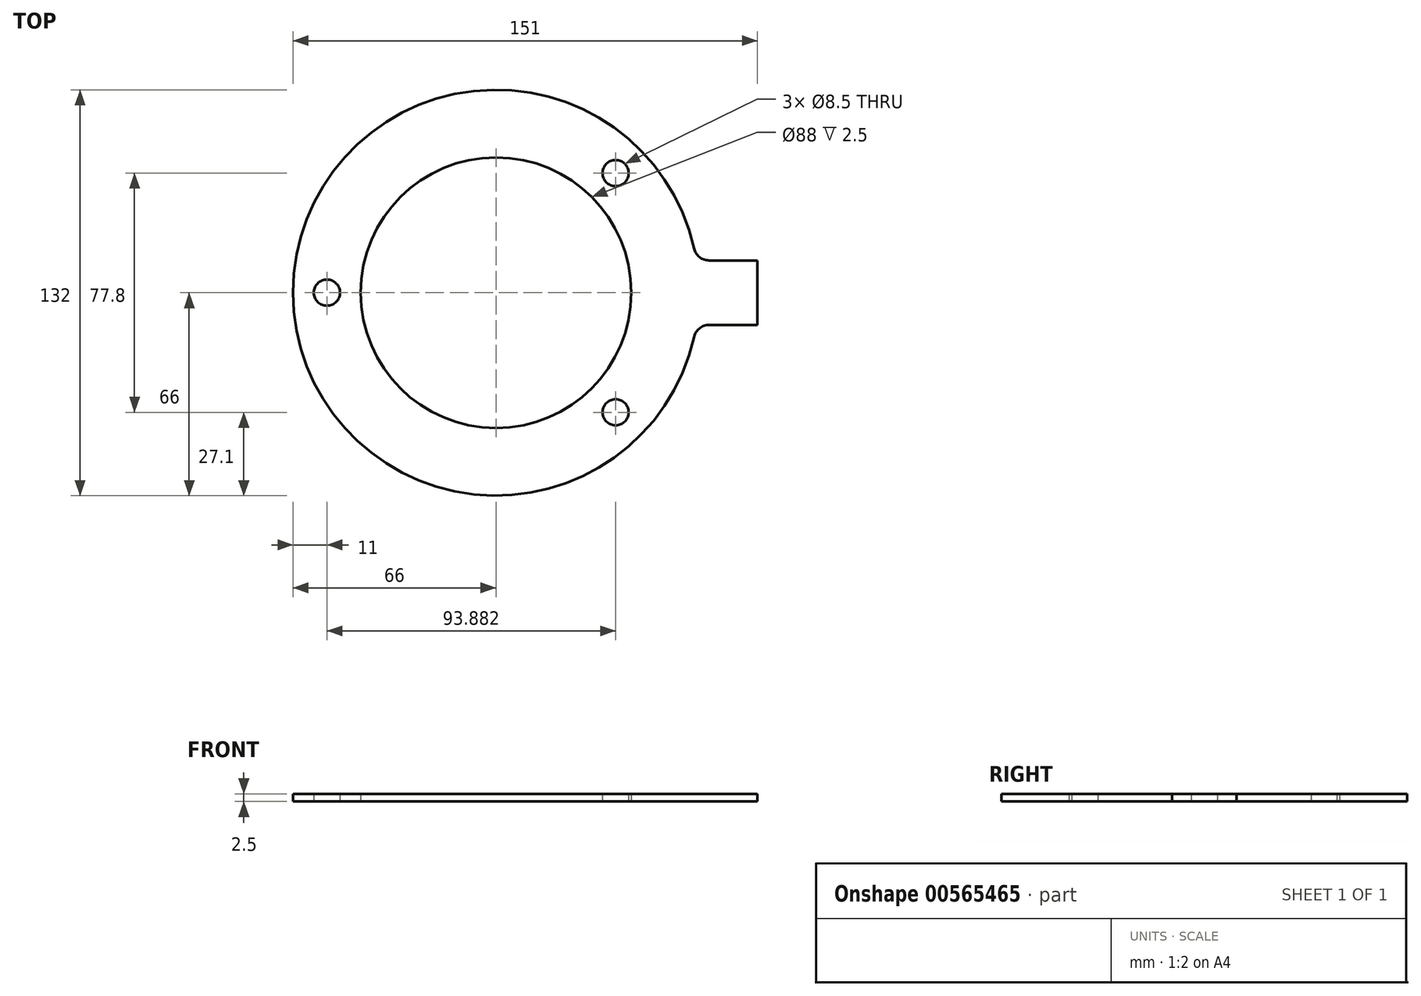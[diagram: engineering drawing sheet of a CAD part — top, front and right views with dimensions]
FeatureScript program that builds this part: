
annotation { "Feature Type Name" : "Feature", "Feature Type Description" : "" }
export const myFeature = defineFeature(function(context is Context, id is Id, definition is map)
    precondition{}
    {
        {
            var Q0;
            Q0=qCreatedBy(makeId("Top.planeOp"),FACE);
            var sketch = newSketch(context, id + "F0", { "sketchPlane" : qUnion([Q0])});
            skCircle(sketch, "E0", {"center": v(0, 0) * mm, "radius": 44 * mm});
            skLineSegment(sketch, "E1", {"start": v(65.16, 10.5) * mm, "end": v(65.16, 10.5) * mm});
            skLineSegment(sketch, "E2", {"start": v(65.16, 10.5) * mm, "end": v(85, 10.5) * mm});
            skLineSegment(sketch, "E3", {"start": v(85, -10.5) * mm, "end": v(65.16, -10.5) * mm});
            skCircle(sketch, "E4", {"center": v(-55, 0) * mm, "radius": 4.25 * mm});
            skCircle(sketch, "E5", {"center": v(38.88, 38.9) * mm, "radius": 4.25 * mm});
            skCircle(sketch, "E6", {"center": v(38.88, -38.9) * mm, "radius": 4.25 * mm});
            skLineSegment(sketch, "E7", {"start": v(85, 10.5) * mm, "end": v(85, -10.5) * mm});
            skArc(sketch, "E8.trimOffspring", {"start": v(65.16, 10.5) * mm, "mid": v(-66, 0) * mm, "end": v(65.16, -10.5) * mm});
            skSolve(sketch);
        }
        {
            var Q0;
            Q0=qSketchRegion(id+"F0",true);
            extrude(context, id + "F1", {"entities" : qUnion([Q0]), "depth" : 2.5 * mm});
        }
        {
            var Q0;
            Q0=makeQuery(id+"F1.opExtrude","SWEPT_EDGE",EDGE,{"disambiguationData":[OSD([sQuery(id+"F0.wireOp",EDGE,"E1"),sQuery(id+"F0.wireOp",EDGE,"29a9f761-fd3d-4543-bb06-a2a983c4ecf8")])]});
            var Q1;
            Q1=makeQuery(id+"F1.opExtrude","SWEPT_EDGE",EDGE,{"disambiguationData":[OSD([sQuery(id+"F0.wireOp",EDGE,"85b28c9f-8e40-448c-90ee-d4046bafcecc"),sQuery(id+"F0.wireOp",EDGE,"E8.trimOffspring")])]});
            fillet(context, id + "F2", {"entities" : qUnion([Q0, Q1]), "radius" : 5 * mm, "tangentPropagation" : true, "allowEdgeOverflow" : false});
        }
    });
